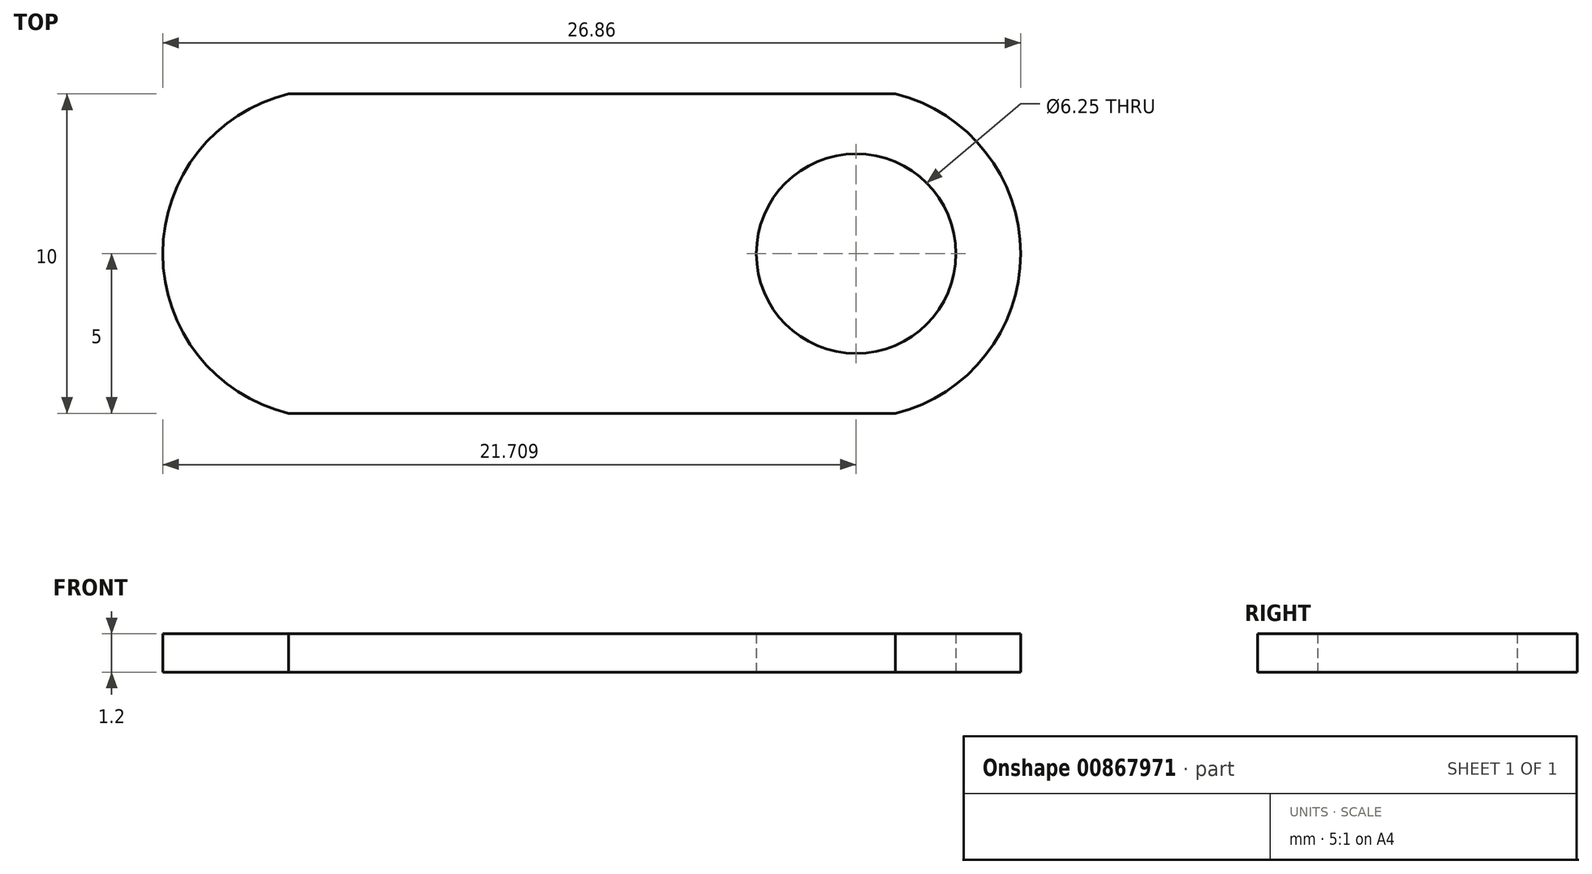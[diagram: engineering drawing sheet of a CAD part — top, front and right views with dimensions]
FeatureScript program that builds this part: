
annotation { "Feature Type Name" : "Feature", "Feature Type Description" : "" }
export const myFeature = defineFeature(function(context is Context, id is Id, definition is map)
    precondition{}
    {
        {
            var Q0;
            Q0=qCreatedBy(makeId("Top.planeOp"),FACE);
            var sketch = newSketch(context, id + "F0", { "sketchPlane" : qUnion([Q0])});
            skLineSegment(sketch, "E0.bottom", {"start": v(9.5, -5) * mm, "end": v(-9.5, -5) * mm});
            skLineSegment(sketch, "E0.top", {"start": v(9.5, 5) * mm, "end": v(-9.5, 5) * mm});
            skPoint(sketch, "E0.middle", {"position": v(0, 0) * mm});
            skLineSegment(sketch, "E1", {"start": v(-13.5, 16.08) * mm, "end": v(-13.5, -14.56) * mm, "construction": true});
            skLineSegment(sketch, "E2", {"start": v(13.5, 17.66) * mm, "end": v(13.5, -14.65) * mm, "construction": true});
            skArc(sketch, "E3", {"start": v(9.5, -5) * mm, "mid": v(13.42, 0) * mm, "end": v(9.5, 5) * mm});
            skArc(sketch, "E4", {"start": v(-9.5, 5) * mm, "mid": v(-13.44, 0) * mm, "end": v(-9.5, -5) * mm});
            skLineSegment(sketch, "E5", {"start": v(11.42, 11.97) * mm, "end": v(11.42, -11.22) * mm, "construction": true});
            skCircle(sketch, "E6", {"center": v(8.27, 0) * mm, "radius": 3.12 * mm});
            skSolve(sketch);
        }
        {
            var Q0;
            Q0=makeQuery(id+"F0.imprint","IMPRINT",FACE,{"disambiguationData":[TD([[makeQuery(id+"F0.imprint","IMPRINT",EDGE,{"derivedFrom":sQuery(id+"F0.wireOp",EDGE,"E0.bottom")}),-1.0]])]});
            extrude(context, id + "F1", {"entities" : qUnion([Q0]), "depth" : 1.2 * mm, "offsetDistance" : 25 * mm});
        }
    });
